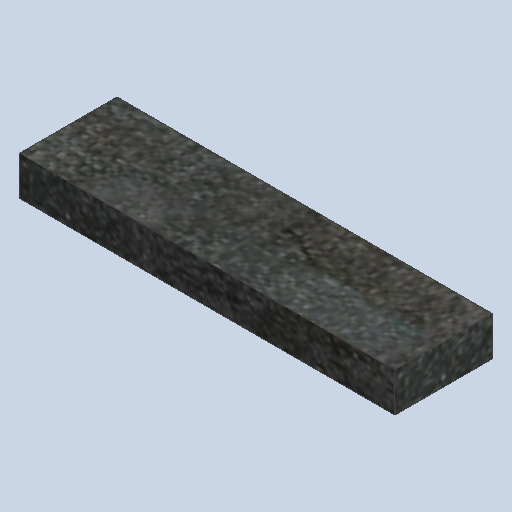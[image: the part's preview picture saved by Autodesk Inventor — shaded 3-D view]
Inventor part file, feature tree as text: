
AUTODESK INVENTOR PART (.ipt)
format: ipt  version: 2023.2 (Build 272271000, 271)  size: 220,672 bytes
history: native  units: mm
features: extrude x2, sketch x2
ambient origin geometry x8: Origin, YZ Plane, XZ Plane, XY Plane, X Axis, Y Axis, Z Axis, Center Point
bodies: Solid1 (feature_tree)
feature tree (4):
  extrude  "Extrusion1"  Depth=20.0mm
  extrude  "Extrusion2"  Depth=2.0mm
  sketch  "Sketch1"  dims[d0=77.0mm d1=20.0mm]
  sketch  "Sketch2"  dims[d2=5.0mm d3=5.0mm d4=55.0mm d5=10.0mm d6=6.0mm d7=0.0mm d8=2.0mm d9=0.0mm]
